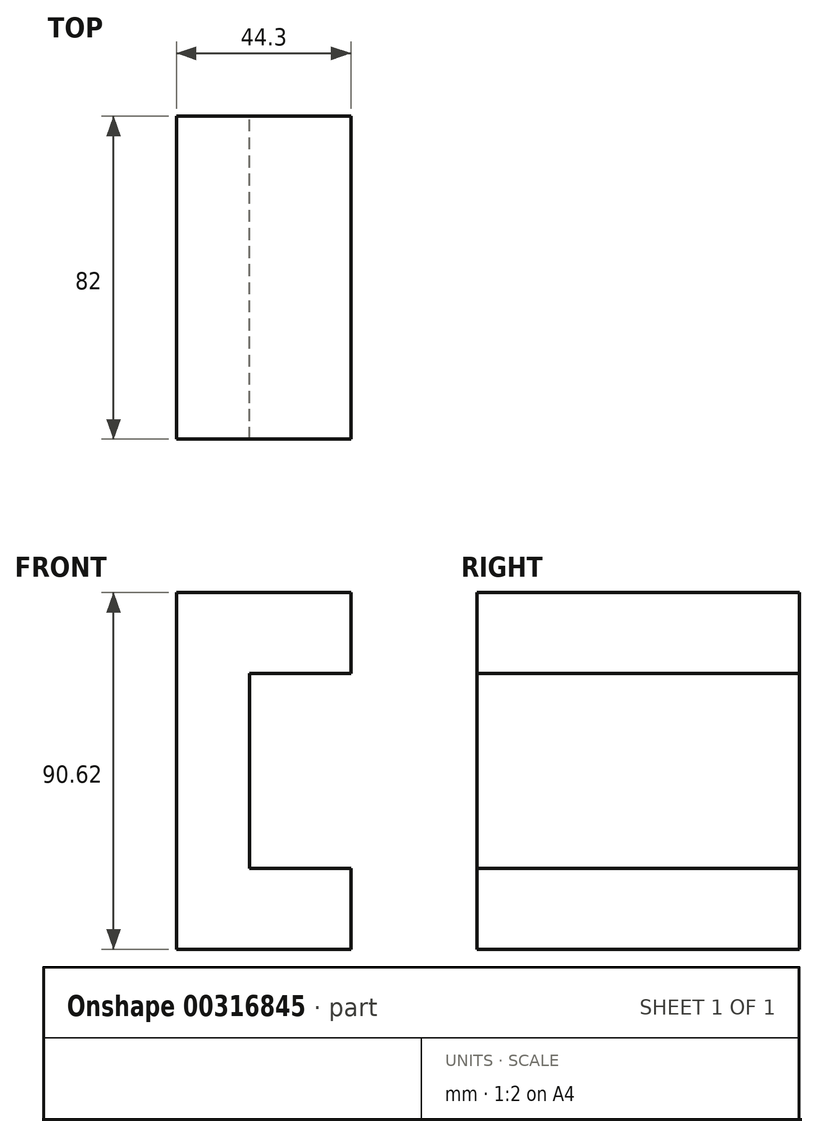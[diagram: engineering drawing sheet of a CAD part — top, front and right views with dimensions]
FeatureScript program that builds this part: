
annotation { "Feature Type Name" : "Feature", "Feature Type Description" : "" }
export const myFeature = defineFeature(function(context is Context, id is Id, definition is map)
    precondition{}
    {
        {
            var Q0;
            Q0=qCreatedBy(makeId("Front.planeOp"),FACE);
            var sketch = newSketch(context, id + "F0", { "sketchPlane" : qUnion([Q0])});
            skLineSegment(sketch, "E0.bottom", {"start": v(-57.88, 45.3) * mm, "end": v(-39.3, 45.3) * mm});
            skLineSegment(sketch, "E0.left", {"start": v(-57.88, 45.3) * mm, "end": v(-57.88, -37.02) * mm});
            skLineSegment(sketch, "E0.right", {"start": v(-39.3, 24.73) * mm, "end": v(-39.3, -24.73) * mm});
            skLineSegment(sketch, "E1.bottom", {"start": v(-39.3, 45.3) * mm, "end": v(-13.58, 45.3) * mm});
            skLineSegment(sketch, "E1.top", {"start": v(-39.3, 24.73) * mm, "end": v(-13.58, 24.73) * mm});
            skLineSegment(sketch, "E1.right", {"start": v(-13.58, 45.3) * mm, "end": v(-13.58, 24.73) * mm});
            skLineSegment(sketch, "E2.MirrorCS", {"start": v(-39.3, -24.73) * mm, "end": v(-13.58, -24.73) * mm});
            skLineSegment(sketch, "E3.MirrorCS", {"start": v(-39.3, -45.3) * mm, "end": v(-13.58, -45.3) * mm});
            skLineSegment(sketch, "E4.MirrorCS", {"start": v(-13.58, -45.3) * mm, "end": v(-13.58, -24.73) * mm});
            skLineSegment(sketch, "E5.MirrorCS", {"start": v(-57.88, -45.3) * mm, "end": v(-57.88, 37.02) * mm});
            skLineSegment(sketch, "E6.MirrorCS", {"start": v(-57.88, -45.3) * mm, "end": v(-39.3, -45.3) * mm});
            skLineSegment(sketch, "E7.trimOffspring", {"start": v(-39.3, -24.73) * mm, "end": v(-39.3, 24.73) * mm});
            skPoint(sketch, "E8.MirrorCS.start.orphan", {"position": v(-39.3, -45.3) * mm});
            skSolve(sketch);
        }
        {
            var Q0;
            Q0=makeQuery(id+"F0.imprint","IMPRINT",FACE,{"disambiguationData":[TD([[makeQuery(id+"F0.imprint","IMPRINT",EDGE,{"derivedFrom":sQuery(id+"F0.wireOp",EDGE,"E0.bottom")}),-1.0]])]});
            extrude(context, id + "F1", {"entities" : qUnion([Q0]), "endBound" : BoundingType.SYMMETRIC, "depth" : 82 * mm});
        }
    });
